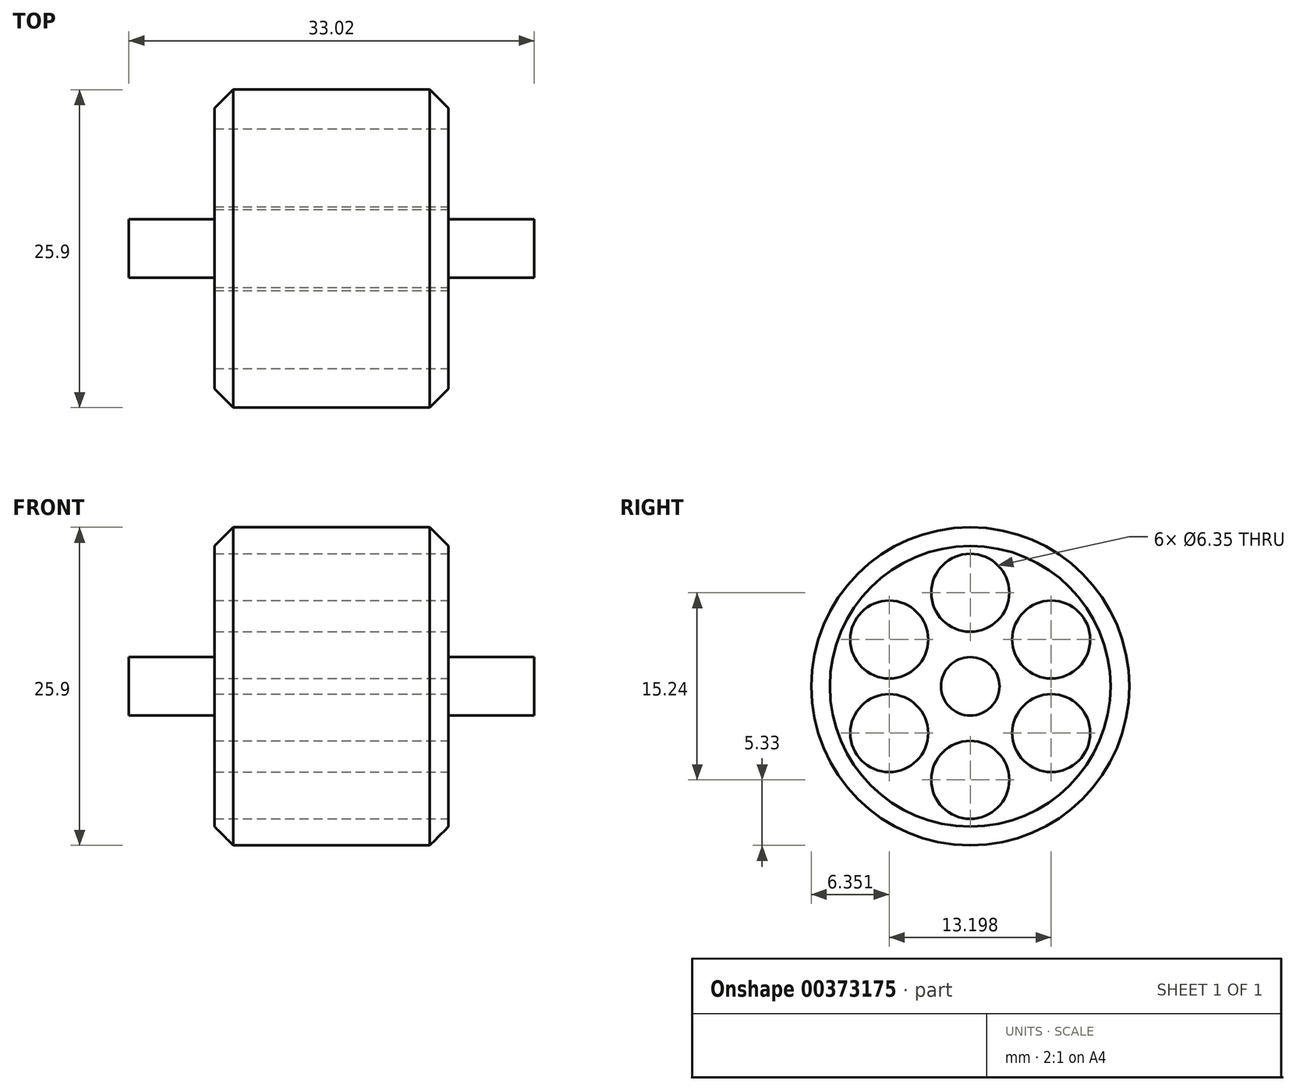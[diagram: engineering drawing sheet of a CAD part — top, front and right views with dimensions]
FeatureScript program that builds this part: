
annotation { "Feature Type Name" : "Feature", "Feature Type Description" : "" }
export const myFeature = defineFeature(function(context is Context, id is Id, definition is map)
    precondition{}
    {
        {
            var Q0;
            Q0=qCreatedBy(makeId("Right.planeOp"),FACE);
            var sketch = newSketch(context, id + "F0", { "sketchPlane" : qUnion([Q0])});
            skCircle(sketch, "E0", {"center": v(0, 0) * mm, "radius": 12.95 * mm});
            skCircle(sketch, "E1", {"center": v(0, 0) * mm, "radius": 2.38 * mm});
            skSolve(sketch);
        }
        {
            var Q0;
            Q0=makeQuery(id+"F0.imprint","IMPRINT",FACE,{"disambiguationData":[TD([[makeQuery(id+"F0.imprint","IMPRINT",EDGE,{"derivedFrom":sQuery(id+"F0.wireOp",EDGE,"E0")}),1.0]])]});
            extrude(context, id + "F1", {"entities" : qUnion([Q0]), "depth" : 19.05 * mm, "symmetric" : true});
        }
        {
            var Q0;
            Q0=makeQuery(id+"F0.imprint","IMPRINT",FACE,{"disambiguationData":[TD([[makeQuery(id+"F0.imprint","IMPRINT",EDGE,{"derivedFrom":sQuery(id+"F0.wireOp",EDGE,"E1")}),1.0]])]});
            extrude(context, id + "F2", {"entities" : qUnion([Q0]), "operationType" : NewBodyOperationType.ADD, "depth" : 33.02 * mm, "symmetric" : true});
        }
        {
            var Q0;
            Q0=makeQuery(id+"F1.opExtrude","CAP_FACE",FACE,{"disambiguationData":[OSD([sQuery(id+"F0.wireOp",EDGE,"E0"),sQuery(id+"F0.wireOp",EDGE,"E1")])],"isStart":false});
            var sketch = newSketch(context, id + "F3", { "sketchPlane" : qUnion([Q0])});
            skCircle(sketch, "E2", {"center": v(0, 7.62) * mm, "radius": 3.18 * mm});
            skCircle(sketch, "E3.1.0", {"center": v(-6.6, 3.81) * mm, "radius": 3.18 * mm});
            skCircle(sketch, "E3.2.0", {"center": v(-6.6, -3.8) * mm, "radius": 3.18 * mm});
            skCircle(sketch, "E3.3.0", {"center": v(0, -7.62) * mm, "radius": 3.18 * mm});
            skCircle(sketch, "E3.4.0", {"center": v(6.6, -3.81) * mm, "radius": 3.18 * mm});
            skPoint(sketch, "E3.center", {"position": v(0, 0) * mm});
            skCircle(sketch, "E4.1.5.0", {"center": v(6.6, 3.81) * mm, "radius": 3.18 * mm});
            skSolve(sketch);
        }
        {
            var Q0;
            Q0 = qSketchRegion(id + "F3", true);
            extrude(context, id + "F4", {"entities" : qUnion([Q0]), "operationType" : NewBodyOperationType.REMOVE, "endBound" : BoundingType.THROUGH_ALL, "oppositeDirection" : true, "depth" : 25.4 * mm});
        }
        {
            var Q0;
            Q0=makeQuery(id+"F1.opExtrude","CAP_EDGE",EDGE,{"disambiguationData":[OSD([sQuery(id+"F0.wireOp",EDGE,"E0")])],"isStart":false});
            var Q1;
            Q1=makeQuery(id+"F1.opExtrude","CAP_EDGE",EDGE,{"disambiguationData":[OSD([sQuery(id+"F0.wireOp",EDGE,"E0")])],"isStart":true});
            chamfer(context, id + "F5", {"entities" : qUnion([Q0, Q1]), "width" : 1.52 * mm, "tangentPropagation" : true});
        }
    });
